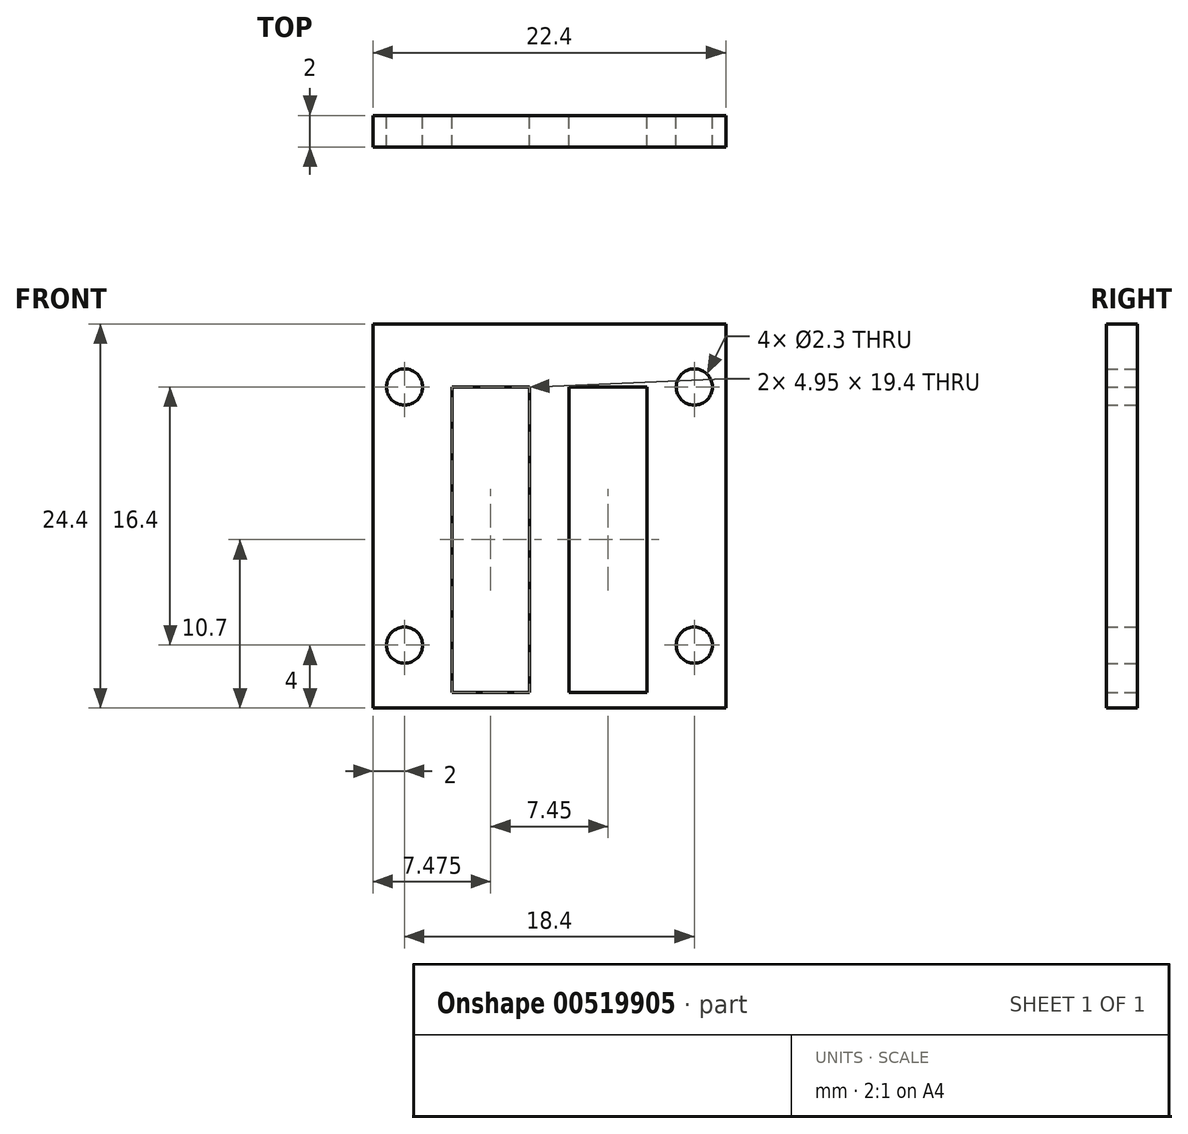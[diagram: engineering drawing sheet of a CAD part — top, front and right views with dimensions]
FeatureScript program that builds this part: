
annotation { "Feature Type Name" : "Feature", "Feature Type Description" : "" }
export const myFeature = defineFeature(function(context is Context, id is Id, definition is map)
    precondition{}
    {
        {
            var Q0;
            Q0=qCreatedBy(makeId("Front.planeOp"),FACE);
            var sketch = newSketch(context, id + "F0", { "sketchPlane" : qUnion([Q0])});
            skLineSegment(sketch, "E0", {"start": v(11.2, 1) * mm, "end": v(11.2, 20.4) * mm, "construction": true});
            skLineSegment(sketch, "E1", {"start": v(11.2, 1) * mm, "end": v(16.2, 1) * mm, "construction": true});
            skLineSegment(sketch, "E2.MirrorCS", {"start": v(11.2, 1) * mm, "end": v(6.2, 1) * mm, "construction": true});
            skLineSegment(sketch, "E3", {"start": v(16.2, 1) * mm, "end": v(16.2, 0) * mm});
            skLineSegment(sketch, "E4", {"start": v(16.2, 0) * mm, "end": v(14.7, 0) * mm});
            skLineSegment(sketch, "E5", {"start": v(14.7, 0) * mm, "end": v(14.7, 1) * mm});
            skLineSegment(sketch, "E6", {"start": v(14.7, 1) * mm, "end": v(16.2, 1) * mm});
            skLineSegment(sketch, "E7.MirrorCS", {"start": v(7.7, 0) * mm, "end": v(7.7, 1) * mm});
            skLineSegment(sketch, "E8.MirrorCS", {"start": v(7.7, 1) * mm, "end": v(6.2, 1) * mm});
            skLineSegment(sketch, "E9.MirrorCS", {"start": v(6.2, 1) * mm, "end": v(6.2, 0) * mm});
            skLineSegment(sketch, "E10.MirrorCS", {"start": v(6.2, 0) * mm, "end": v(7.7, 0) * mm});
            skLineSegment(sketch, "E11", {"start": v(11.2, 20.4) * mm, "end": v(12.45, 20.4) * mm});
            skLineSegment(sketch, "E12", {"start": v(12.45, 20.4) * mm, "end": v(12.45, 22.4) * mm});
            skLineSegment(sketch, "E13.MirrorCS", {"start": v(9.95, 20.4) * mm, "end": v(9.95, 22.4) * mm});
            skLineSegment(sketch, "E14.MirrorCS", {"start": v(11.2, 20.4) * mm, "end": v(9.95, 20.4) * mm});
            skLineSegment(sketch, "E15", {"start": v(12.45, 22.4) * mm, "end": v(11.2, 22.4) * mm});
            skLineSegment(sketch, "E16.MirrorCS", {"start": v(9.95, 22.4) * mm, "end": v(11.2, 22.4) * mm});
            skLineSegment(sketch, "E17", {"start": v(12.45, 1) * mm, "end": v(12.45, 20.4) * mm});
            skLineSegment(sketch, "E18.MirrorCS", {"start": v(9.95, 1) * mm, "end": v(9.95, 20.4) * mm});
            skLineSegment(sketch, "E19", {"start": v(11.2, 1) * mm, "end": v(14.7, 1) * mm});
            skLineSegment(sketch, "E20.MirrorCS", {"start": v(11.2, 1) * mm, "end": v(7.7, 1) * mm});
            skLineSegment(sketch, "E21", {"start": v(7.7, 0) * mm, "end": v(14.7, 0) * mm});
            skLineSegment(sketch, "E22", {"start": v(16.2, 1) * mm, "end": v(17.4, 1) * mm});
            skLineSegment(sketch, "E23", {"start": v(17.4, 1) * mm, "end": v(17.4, 0) * mm});
            skLineSegment(sketch, "E24", {"start": v(17.4, 0) * mm, "end": v(16.2, 0) * mm});
            skLineSegment(sketch, "E25", {"start": v(17.4, 0) * mm, "end": v(18.4, 0) * mm});
            skLineSegment(sketch, "E26", {"start": v(18.4, 0) * mm, "end": v(18.4, 22.4) * mm});
            skLineSegment(sketch, "E27", {"start": v(12.45, 22.4) * mm, "end": v(18.4, 22.4) * mm});
            skLineSegment(sketch, "E28", {"start": v(12.45, 20.4) * mm, "end": v(18.4, 20.4) * mm});
            skLineSegment(sketch, "E29", {"start": v(17.4, 1) * mm, "end": v(17.4, 22.4) * mm});
            skLineSegment(sketch, "E30.MirrorCS", {"start": v(9.95, 20.4) * mm, "end": v(4, 20.4) * mm});
            skLineSegment(sketch, "E31.MirrorCS", {"start": v(5, 1) * mm, "end": v(5, 22.4) * mm});
            skLineSegment(sketch, "E32.MirrorCS", {"start": v(4, 0) * mm, "end": v(4, 22.4) * mm});
            skLineSegment(sketch, "E33.MirrorCS", {"start": v(9.95, 22.4) * mm, "end": v(4, 22.4) * mm});
            skLineSegment(sketch, "E34.MirrorCS", {"start": v(6.2, 1) * mm, "end": v(5, 1) * mm});
            skLineSegment(sketch, "E35.MirrorCS", {"start": v(5, 1) * mm, "end": v(5, 0) * mm});
            skLineSegment(sketch, "E36.MirrorCS", {"start": v(5, 0) * mm, "end": v(4, 0) * mm});
            skLineSegment(sketch, "E37.MirrorCS", {"start": v(5, 0) * mm, "end": v(6.2, 0) * mm});
            skLineSegment(sketch, "E38", {"start": v(11.2, 22.4) * mm, "end": v(11.2, 24.4) * mm});
            skLineSegment(sketch, "E39", {"start": v(11.2, 24.4) * mm, "end": v(22.4, 24.4) * mm});
            skLineSegment(sketch, "E40", {"start": v(18.4, 22.4) * mm, "end": v(22.4, 22.4) * mm});
            skLineSegment(sketch, "E41", {"start": v(22.4, 22.4) * mm, "end": v(22.4, 18.4) * mm});
            skLineSegment(sketch, "E42", {"start": v(22.4, 18.4) * mm, "end": v(18.4, 18.4) * mm});
            skLineSegment(sketch, "E43", {"start": v(18.4, 0) * mm, "end": v(22.4, 0) * mm});
            skLineSegment(sketch, "E44", {"start": v(22.4, 0) * mm, "end": v(22.4, 2) * mm});
            skLineSegment(sketch, "E45", {"start": v(18.4, 22.4) * mm, "end": v(22.4, 18.4) * mm, "construction": true});
            skCircle(sketch, "E46", {"center": v(20.4, 20.4) * mm, "radius": 1.15 * mm});
            skLineSegment(sketch, "E47.MirrorCS", {"start": v(0, 18.4) * mm, "end": v(4, 18.4) * mm});
            skCircle(sketch, "E48.MirrorC", {"center": v(2, 20.4) * mm, "radius": 1.15 * mm});
            skLineSegment(sketch, "E49.MirrorCS", {"start": v(0, 22.4) * mm, "end": v(0, 18.4) * mm});
            skLineSegment(sketch, "E50.MirrorCS", {"start": v(4, 22.4) * mm, "end": v(0, 22.4) * mm});
            skLineSegment(sketch, "E51.MirrorCS", {"start": v(0, 0) * mm, "end": v(0, 2) * mm});
            skLineSegment(sketch, "E52.MirrorCS", {"start": v(4, 0) * mm, "end": v(0, 0) * mm});
            skLineSegment(sketch, "E53", {"start": v(22.4, 18.4) * mm, "end": v(22.4, 2) * mm});
            skLineSegment(sketch, "E54.MirrorCS", {"start": v(0, 18.4) * mm, "end": v(0, 2) * mm});
            skLineSegment(sketch, "E55", {"start": v(11.2, 23.4) * mm, "end": v(22.4, 23.4) * mm, "construction": true});
            skLineSegment(sketch, "E56.MirrorCS", {"start": v(11.2, 24.4) * mm, "end": v(0, 24.4) * mm});
            skLineSegment(sketch, "E57", {"start": v(22.4, 24.4) * mm, "end": v(22.4, 22.4) * mm});
            skLineSegment(sketch, "E58.MirrorCS", {"start": v(0, 24.4) * mm, "end": v(0, 22.4) * mm});
            skLineSegment(sketch, "E59", {"start": v(0, 22.4) * mm, "end": v(0, 24.4) * mm});
            skLineSegment(sketch, "E60", {"start": v(0, 24.4) * mm, "end": v(4, 24.4) * mm});
            skLineSegment(sketch, "E61.MirrorCS", {"start": v(22.4, 24.4) * mm, "end": v(18.4, 24.4) * mm});
            skLineSegment(sketch, "E62.MirrorCS", {"start": v(22.4, 22.4) * mm, "end": v(22.4, 24.4) * mm});
            skLineSegment(sketch, "E63", {"start": v(18.4, 22.4) * mm, "end": v(18.4, 24.4) * mm});
            skLineSegment(sketch, "E64", {"start": v(17.4, 24.4) * mm, "end": v(17.4, 22.4) * mm});
            skLineSegment(sketch, "E65", {"start": v(17.4, 24.4) * mm, "end": v(18.4, 24.4) * mm});
            skLineSegment(sketch, "E66.MirrorCS", {"start": v(5, 24.4) * mm, "end": v(5, 22.4) * mm});
            skLineSegment(sketch, "E67.MirrorCS", {"start": v(5, 24.4) * mm, "end": v(4, 24.4) * mm});
            skLineSegment(sketch, "E68.MirrorCS", {"start": v(4, 22.4) * mm, "end": v(4, 24.4) * mm});
            skLineSegment(sketch, "E69", {"start": v(22.4, 22.4) * mm, "end": v(22.4, 2) * mm, "construction": true});
            skLineSegment(sketch, "E70", {"start": v(22.4, 12.2) * mm, "end": v(27.65, 12.2) * mm, "construction": true});
            skCircle(sketch, "E71.MirrorC", {"center": v(20.4, 4) * mm, "radius": 1.15 * mm});
            skLineSegment(sketch, "E72.MirrorCS", {"start": v(22.4, 6) * mm, "end": v(18.4, 6) * mm});
            skLineSegment(sketch, "E73.MirrorCS", {"start": v(18.4, 2) * mm, "end": v(22.4, 2) * mm});
            skLineSegment(sketch, "E74.MirrorCS", {"start": v(0, 6) * mm, "end": v(4, 6) * mm});
            skCircle(sketch, "E75.MirrorC", {"center": v(2, 4) * mm, "radius": 1.15 * mm});
            skLineSegment(sketch, "E76.MirrorCS", {"start": v(4, 2) * mm, "end": v(0, 2) * mm});
            skLineSegment(sketch, "E77", {"start": v(11.2, 13.59) * mm, "end": v(17.4, 13.59) * mm, "construction": true});
            skSolve(sketch);
        }
        {
            var Q0;
            Q0 = qSketchRegion(id + "F0", true);
            var Q1;
            Q1=makeQuery(id+"F0.imprint","IMPRINT",FACE,{"disambiguationData":[TD([[makeQuery(id+"F0.imprint","IMPRINT",EDGE,{"derivedFrom":sQuery(id+"F0.wireOp",EDGE,"E11")}),-1.0]])]});
            var Q2;
            {var subQ0=sQuery(id+"F0.wireOp",EDGE,"E13.MirrorCS");Q2=makeQuery(id+"F0.imprint","IMPRINT",FACE,{"disambiguationData":[TD([[makeQuery(id+"F0.imprint","IMPRINT",EDGE,{"derivedFrom":subQ0}),1.0]])]});}
            var Q3;
            {var subQ0=sQuery(id+"F0.wireOp",EDGE,"E32.MirrorCS");var subQ1=sQuery(id+"F0.wireOp",EDGE,"E30.MirrorCS");var subQ2=makeQuery(id+"F0.imprint","INTERSECT",VERTEX,{"derivedFrom":[subQ1,subQ0]});Q3=makeQuery(id+"F0.imprint","IMPRINT",FACE,{"disambiguationData":[TD([[makeQuery(id+"F0.imprint","IMPRINT",EDGE,{"disambiguationData":[TD([[subQ2,1.0]])],"derivedFrom":subQ1}),-1.0]])]});}
            var Q4;
            Q4=makeQuery(id+"F0.imprint","IMPRINT",FACE,{"disambiguationData":[TD([[makeQuery(id+"F0.imprint","IMPRINT",EDGE,{"derivedFrom":sQuery(id+"F0.wireOp",EDGE,"E11")}),1.0]])]});
            var Q5;
            {var subQ1=sQuery(id+"F0.wireOp",EDGE,"E26");var subQ3=sQuery(id+"F0.wireOp",EDGE,"E28");var subQ4=makeQuery(id+"F0.imprint","INTERSECT",VERTEX,{"derivedFrom":[subQ1,subQ3]});Q5=makeQuery(id+"F0.imprint","IMPRINT",FACE,{"disambiguationData":[TD([[makeQuery(id+"F0.imprint","IMPRINT",EDGE,{"disambiguationData":[TD([[subQ4,1.0]])],"derivedFrom":subQ3}),1.0]])]});}
            var Q6;
            {var subQ0=sQuery(id+"F0.wireOp",EDGE,"E12");Q6=makeQuery(id+"F0.imprint","IMPRINT",FACE,{"disambiguationData":[TD([[makeQuery(id+"F0.imprint","IMPRINT",EDGE,{"derivedFrom":subQ0}),-1.0]])]});}
            extrude(context, id + "F1", {"entities" : qUnion([Q0, Q1, Q2, Q3, Q4, Q5, Q6]), "depth" : 2 * mm, "offsetDistance" : 25 * mm});
        }
    });
